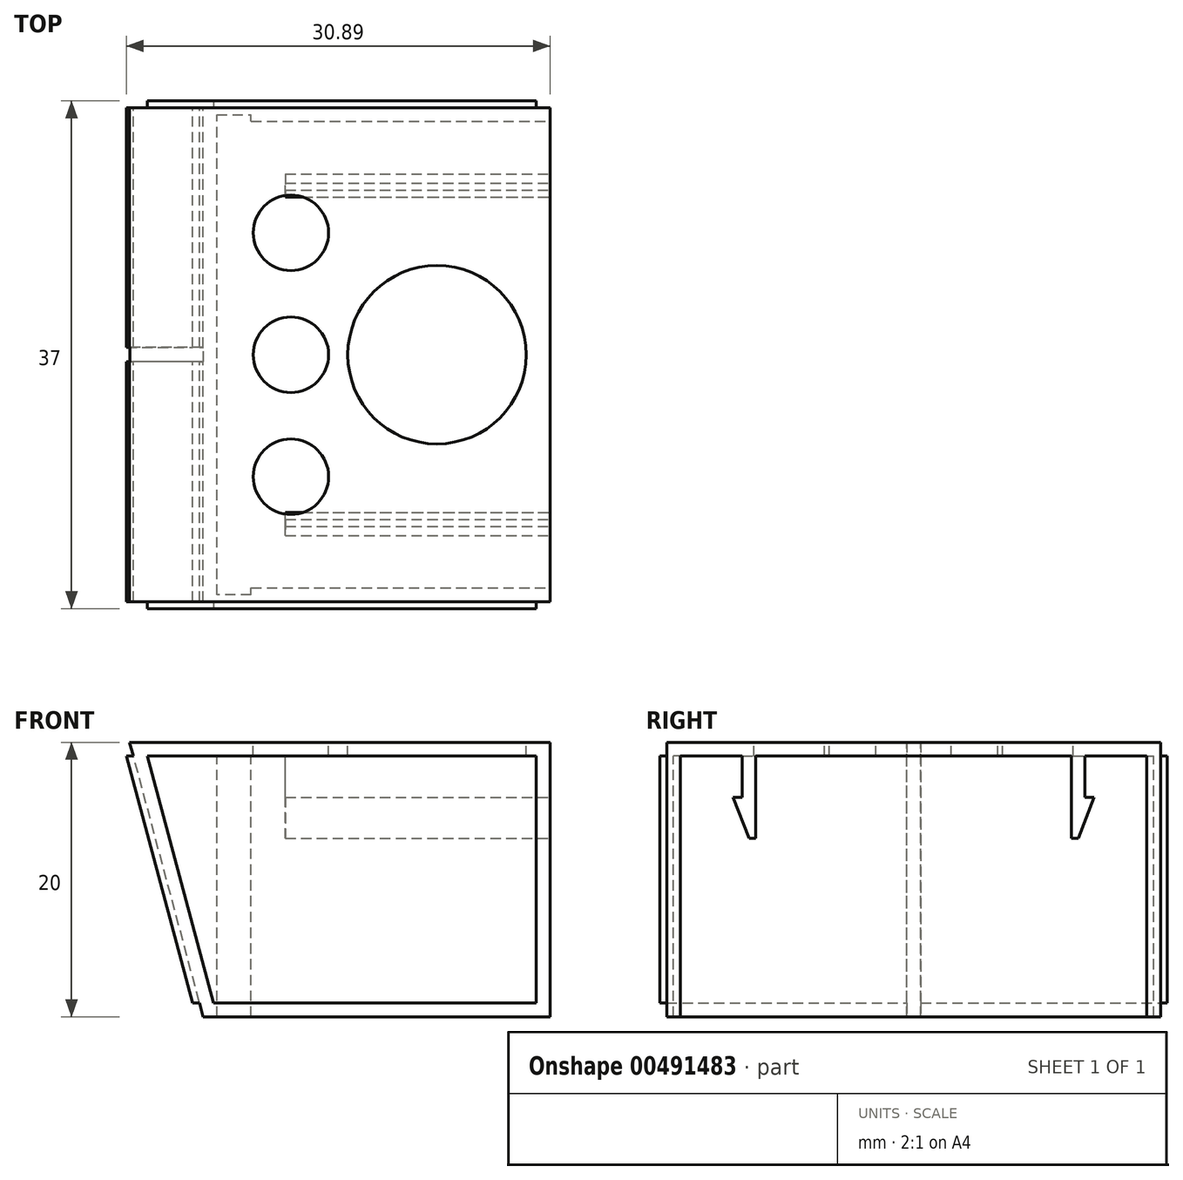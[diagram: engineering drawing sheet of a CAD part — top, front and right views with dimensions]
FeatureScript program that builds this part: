
annotation { "Feature Type Name" : "Feature", "Feature Type Description" : "" }
export const myFeature = defineFeature(function(context is Context, id is Id, definition is map)
    precondition{}
    {
        {
            var Q0;
            Q0=qCreatedBy(makeId("Right.planeOp"),FACE);
            var sketch = newSketch(context, id + "F0", { "sketchPlane" : qUnion([Q0])});
            skLineSegment(sketch, "E0.0", {"start": v(-0.5, 0) * mm, "end": v(-0.5, 19) * mm});
            skLineSegment(sketch, "E1.0", {"start": v(-34.5, 0) * mm, "end": v(-34.5, 19) * mm});
            skLineSegment(sketch, "E2", {"start": v(-34.5, 19) * mm, "end": v(-0.5, 19) * mm});
            skLineSegment(sketch, "E3", {"start": v(-34.5, 0) * mm, "end": v(-0.5, 0) * mm});
            skLineSegment(sketch, "E4.MirrorCS", {"start": v(-30, 16) * mm, "end": v(-30, 19) * mm});
            skLineSegment(sketch, "E5.MirrorCS", {"start": v(-30.67, 16) * mm, "end": v(-30, 16) * mm});
            skLineSegment(sketch, "E6.MirrorCS", {"start": v(-29.5, 13) * mm, "end": v(-30.67, 16) * mm});
            skLineSegment(sketch, "E7.MirrorCS", {"start": v(-29.5, 13) * mm, "end": v(-29, 13) * mm});
            skLineSegment(sketch, "E8.MirrorCS", {"start": v(-29, 13) * mm, "end": v(-29, 19) * mm});
            skLineSegment(sketch, "E9.MirrorCS", {"start": v(-4.33, 16) * mm, "end": v(-5.5, 13) * mm});
            skLineSegment(sketch, "E10.MirrorCS", {"start": v(-4.33, 16) * mm, "end": v(-5, 16) * mm});
            skLineSegment(sketch, "E11.MirrorCS", {"start": v(-5, 16) * mm, "end": v(-5, 19) * mm});
            skLineSegment(sketch, "E12.MirrorCS", {"start": v(-5.5, 13) * mm, "end": v(-6, 13) * mm});
            skLineSegment(sketch, "E13.MirrorCS", {"start": v(-6, 13) * mm, "end": v(-6, 19) * mm});
            skSolve(sketch);
        }
        {
            var Q0;
            Q0=qCreatedBy(makeId("Front.planeOp"),FACE);
            var sketch = newSketch(context, id + "F1", { "sketchPlane" : qUnion([Q0])});
            skLineSegment(sketch, "E14", {"start": v(0, 0) * mm, "end": v(-25.3, 0) * mm});
            skLineSegment(sketch, "E15", {"start": v(-25.3, 0) * mm, "end": v(-30.66, 20) * mm});
            skLineSegment(sketch, "E16", {"start": v(-30.66, 20) * mm, "end": v(0, 20) * mm});
            skLineSegment(sketch, "E17", {"start": v(0, 20) * mm, "end": v(0, 0) * mm});
            skLineSegment(sketch, "E18", {"start": v(-25.3, 0) * mm, "end": v(-38.12, 0) * mm});
            skLineSegment(sketch, "E19", {"start": v(-30.9, 19) * mm, "end": v(-26.07, 1) * mm});
            skPoint(sketch, "E20.orphan", {"position": v(-25.3, -1.87) * mm});
            skLineSegment(sketch, "E21", {"start": v(0, 19) * mm, "end": v(0, 19) * mm});
            skLineSegment(sketch, "E22", {"start": v(-26.07, 1) * mm, "end": v(-25.57, 1) * mm});
            skPoint(sketch, "E23.0.start.orphan", {"position": v(0, 1) * mm});
            skPoint(sketch, "E24.orphan", {"position": v(-29.4, 1) * mm});
            skLineSegment(sketch, "E25", {"start": v(-30.9, 19) * mm, "end": v(-30.4, 19) * mm});
            skLineSegment(sketch, "E26.0", {"start": v(-30.66, 19) * mm, "end": v(-30.4, 19) * mm});
            skLineSegment(sketch, "E27.0", {"start": v(-24.53, 1) * mm, "end": v(-29.36, 19) * mm});
            skLineSegment(sketch, "E28.0", {"start": v(-1, 1) * mm, "end": v(-24.53, 1) * mm});
            skLineSegment(sketch, "E29.0", {"start": v(-1, 19) * mm, "end": v(-1, 1) * mm});
            skLineSegment(sketch, "E30.trimOffspring", {"start": v(-29.36, 19) * mm, "end": v(-1, 19) * mm});
            skLineSegment(sketch, "E31", {"start": v(-30.66, 20) * mm, "end": v(-37.02, 18.3) * mm});
            skSolve(sketch);
        }
        {
            var Q0;
            Q0=makeQuery(id+"F1.imprint","IMPRINT",FACE,{"disambiguationData":[TD([[makeQuery(id+"F1.imprint","IMPRINT",EDGE,{"derivedFrom":sQuery(id+"F1.wireOp",EDGE,"E14")}),-1.0]])]});
            var Q1;
            Q1=makeQuery(id+"F1.imprint","IMPRINT",FACE,{"disambiguationData":[TD([[makeQuery(id+"F1.imprint","IMPRINT",EDGE,{"derivedFrom":sQuery(id+"F1.wireOp",EDGE,"E27.0")}),-1.0]])]});
            var Q2;
            Q2=makeQuery(id+"F1.imprint","IMPRINT",FACE,{"disambiguationData":[TD([[makeQuery(id+"F1.imprint","IMPRINT",EDGE,{"derivedFrom":sQuery(id+"F1.wireOp",EDGE,"E19")}),1.0]])]});
            extrude(context, id + "F2", {"entities" : qUnion([Q0, Q1, Q2]), "depth" : 35.5 * mm, "hasSecondDirection" : true, "secondDirectionOppositeDirection" : true, "secondDirectionDepth" : 0.5 * mm});
        }
        {
            var Q0;
            Q0=makeQuery(id+"F1.imprint","IMPRINT",FACE,{"disambiguationData":[TD([[makeQuery(id+"F1.imprint","IMPRINT",EDGE,{"derivedFrom":sQuery(id+"F1.wireOp",EDGE,"E27.0")}),-1.0]])]});
            extrude(context, id + "F3", {"entities" : qUnion([Q0]), "operationType" : NewBodyOperationType.ADD, "oppositeDirection" : true, "depth" : 1 * mm, "hasSecondDirection" : true, "secondDirectionOppositeDirection" : false, "secondDirectionDepth" : 36 * mm});
        }
        {
            var Q0;
            Q0=makeQuery(id+"F0.imprint","IMPRINT",FACE,{"disambiguationData":[TD([[makeQuery(id+"F0.imprint","IMPRINT",EDGE,{"derivedFrom":sQuery(id+"F0.wireOp",EDGE,"32d8cbf2-fb97-4c8f-9446-bffa937a5d3c.0")}),1.0]])]});
            var Q1;
            {var subQ3=sQuery(id+"F0.wireOp",EDGE,"E0.0");Q1=makeQuery(id+"F0.imprint","IMPRINT",FACE,{"disambiguationData":[TD([[makeQuery(id+"F0.imprint","IMPRINT",EDGE,{"derivedFrom":subQ3}),1.0]])]});}
            extrude(context, id + "F4", {"entities" : qUnion([Q0, Q1]), "operationType" : NewBodyOperationType.REMOVE, "oppositeDirection" : true, "depth" : 24.3 * mm});
        }
        {
            var Q0;
            Q0=sQuery(id+"F1.wireOp",VERTEX,"E31.end");
            var Q1;
            Q1=sQuery(id+"F1.wireOp",VERTEX,"E16.start");
            var Q2;
            Q2=makeQuery(id+"F2.opExtrude","CAP_VERTEX",VERTEX,{"disambiguationData":[OSD([sQuery(id+"F1.wireOp",EDGE,"E15"),sQuery(id+"F1.wireOp",EDGE,"E16")])],"isStart":false});
            cPlane(context, id + "F5", {"entities" : qUnion([Q0, Q1, Q2]), "cplaneType" : CPlaneType.THREE_POINT, "offset" : 25 * mm, "width" : 150 * mm, "height" : 150 * mm});
        }
        {
            var Q0;
            Q0=qCreatedBy(id+"F5.planeOp",FACE);
            var sketch = newSketch(context, id + "F6", { "sketchPlane" : qUnion([Q0])});
            skLineSegment(sketch, "E32.0", {"start": v(-24.43, -1) * mm, "end": v(-24.93, -1) * mm});
            skLineSegment(sketch, "E33.0", {"start": v(-24.43, -34) * mm, "end": v(-24.93, -34) * mm});
            skLineSegment(sketch, "E34.0", {"start": v(-24.43, -16.97) * mm, "end": v(-24.93, -16.97) * mm});
            skLineSegment(sketch, "E35.0", {"start": v(-24.43, -18) * mm, "end": v(-24.93, -18) * mm});
            skLineSegment(sketch, "E36.trimOffspring", {"start": v(-24.93, -16.97) * mm, "end": v(-24.93, -18) * mm});
            skLineSegment(sketch, "E37.trimOffspring", {"start": v(-24.43, -16.97) * mm, "end": v(-24.43, -18) * mm});
            skLineSegment(sketch, "E38.0", {"start": v(-24.43, 0.5) * mm, "end": v(-24.93, 0.5) * mm});
            skLineSegment(sketch, "E39", {"start": v(-24.93, 0.5) * mm, "end": v(-24.93, -1) * mm});
            skLineSegment(sketch, "E40", {"start": v(-24.43, -1) * mm, "end": v(-24.43, 0.5) * mm});
            skLineSegment(sketch, "E41.0", {"start": v(-24.43, -35.5) * mm, "end": v(-24.93, -35.5) * mm});
            skLineSegment(sketch, "E42", {"start": v(-24.93, -34) * mm, "end": v(-24.93, -35.5) * mm});
            skLineSegment(sketch, "E43", {"start": v(-24.43, -35.5) * mm, "end": v(-24.43, -34) * mm});
            skSolve(sketch);
        }
        {
            var Q0;
            Q0=makeQuery(id+"F6.imprint","IMPRINT",FACE,{"disambiguationData":[TD([[makeQuery(id+"F6.imprint","IMPRINT",EDGE,{"derivedFrom":sQuery(id+"F6.wireOp",EDGE,"9PfR2qlM-xlqo-y65q-UvL4-z1dMFV8YH0sN")}),-1.0]])]});
            var Q1;
            Q1=makeQuery(id+"F6.imprint","IMPRINT",FACE,{"disambiguationData":[TD([[makeQuery(id+"F6.imprint","IMPRINT",EDGE,{"derivedFrom":sQuery(id+"F6.wireOp",EDGE,"E34.0")}),1.0]])]});
            var Q2;
            Q2=makeQuery(id+"F6.imprint","IMPRINT",FACE,{"disambiguationData":[TD([[makeQuery(id+"F6.imprint","IMPRINT",EDGE,{"derivedFrom":sQuery(id+"F6.wireOp",EDGE,"ddf47fad-d214-44eb-bef5-dcffc066888e.0")}),-1.0]])]});
            extrude(context, id + "F7", {"entities" : qUnion([Q0, Q1, Q2]), "operationType" : NewBodyOperationType.REMOVE, "oppositeDirection" : true, "depth" : 25 * mm});
        }
        {
            var Q0;
            Q0=makeQuery(id+"F2.opExtrude","SWEPT_FACE",FACE,{"disambiguationData":[OSD([sQuery(id+"F1.wireOp",EDGE,"E16")])]});
            var sketch = newSketch(context, id + "F8", { "sketchPlane" : qUnion([Q0])});
            skLineSegment(sketch, "E44", {"start": v(0, 0.5) * mm, "end": v(0, -35.5) * mm});
            skLineSegment(sketch, "E45.0", {"start": v(-24.3, 0) * mm, "end": v(-24.3, -35) * mm});
            skLineSegment(sketch, "E46.0", {"start": v(-20.3, -7.34) * mm, "end": v(-20.3, -9.88) * mm});
            skLineSegment(sketch, "E47.0", {"start": v(-18.9, -7.34) * mm, "end": v(-18.9, -9.88) * mm});
            skLineSegment(sketch, "E48", {"start": v(-20.3, -17.5) * mm, "end": v(-18.9, -17.5) * mm});
            skLineSegment(sketch, "E49.0", {"start": v(-20.3, -9.88) * mm, "end": v(-18.9, -9.88) * mm});
            skLineSegment(sketch, "E50.0", {"start": v(-20.3, -25.12) * mm, "end": v(-18.9, -25.12) * mm});
            skLineSegment(sketch, "E51.0", {"start": v(-20.3, -7.34) * mm, "end": v(-18.9, -7.34) * mm});
            skLineSegment(sketch, "E52.0", {"start": v(-20.3, -27.66) * mm, "end": v(-18.9, -27.66) * mm});
            skPoint(sketch, "E53.orphan", {"position": v(-18.9, 0) * mm});
            skPoint(sketch, "E54.orphan", {"position": v(-20.3, 0) * mm});
            skLineSegment(sketch, "E55.trimOffspring", {"start": v(-20.3, -25.12) * mm, "end": v(-20.3, -27.66) * mm});
            skLineSegment(sketch, "E56.trimOffspring", {"start": v(-18.9, -25.12) * mm, "end": v(-18.9, -27.66) * mm});
            skPoint(sketch, "E57.orphan", {"position": v(-20.3, -35) * mm});
            skPoint(sketch, "E58.orphan", {"position": v(-18.9, -35) * mm});
            skCircle(sketch, "E59", {"center": v(-18.9, -26.39) * mm, "radius": 2.75 * mm});
            skCircle(sketch, "E60", {"center": v(-18.9, -8.61) * mm, "radius": 2.75 * mm});
            skCircle(sketch, "E61", {"center": v(-18.9, -17.5) * mm, "radius": 2.75 * mm});
            skLineSegment(sketch, "E62", {"start": v(-18.9, -17.5) * mm, "end": v(-8.25, -17.5) * mm});
            skCircle(sketch, "E63", {"center": v(-8.25, -17.5) * mm, "radius": 6.5 * mm});
            skLineSegment(sketch, "E64.0", {"start": v(-21.8, 0) * mm, "end": v(-21.8, -35) * mm});
            skLineSegment(sketch, "E65", {"start": v(-24.3, -35) * mm, "end": v(-21.8, -35) * mm});
            skLineSegment(sketch, "E66", {"start": v(-21.8, 0) * mm, "end": v(-24.3, 0) * mm});
            skLineSegment(sketch, "E67.0", {"start": v(-24.3, -34.5) * mm, "end": v(-21.8, -34.5) * mm});
            skLineSegment(sketch, "E68.0", {"start": v(-21.8, -0.5) * mm, "end": v(-24.3, -0.5) * mm});
            skSolve(sketch);
        }
        {
            var Q0;
            Q0=makeQuery(id+"F8.imprint","IMPRINT",FACE,{"disambiguationData":[TD([[makeQuery(id+"F8.imprint","IMPRINT",EDGE,{"derivedFrom":sQuery(id+"F8.wireOp",EDGE,"E46.0")}),-1.0]])]});
            var Q1;
            Q1=makeQuery(id+"F8.imprint","IMPRINT",FACE,{"disambiguationData":[TD([[makeQuery(id+"F8.imprint","IMPRINT",EDGE,{"derivedFrom":sQuery(id+"F8.wireOp",EDGE,"E46.0")}),1.0]])]});
            var Q2;
            Q2=makeQuery(id+"F8.imprint","IMPRINT",FACE,{"disambiguationData":[TD([[makeQuery(id+"F8.imprint","IMPRINT",EDGE,{"derivedFrom":sQuery(id+"F8.wireOp",EDGE,"E61")}),1.0]])]});
            var Q3;
            Q3=makeQuery(id+"F8.imprint","IMPRINT",FACE,{"disambiguationData":[TD([[makeQuery(id+"F8.imprint","IMPRINT",EDGE,{"derivedFrom":sQuery(id+"F8.wireOp",EDGE,"E50.0")}),1.0]])]});
            var Q4;
            Q4=makeQuery(id+"F8.imprint","IMPRINT",FACE,{"disambiguationData":[TD([[makeQuery(id+"F8.imprint","IMPRINT",EDGE,{"derivedFrom":sQuery(id+"F8.wireOp",EDGE,"E63")}),1.0]])]});
            var Q5;
            Q5=makeQuery(id+"F8.imprint","IMPRINT",FACE,{"disambiguationData":[TD([[makeQuery(id+"F8.imprint","IMPRINT",EDGE,{"derivedFrom":sQuery(id+"F8.wireOp",EDGE,"E50.0")}),-1.0]])]});
            var Q6;
            {var subQ0=sQuery(id+"F0.wireOp",EDGE,"E2");Q6=makeQuery(id+"F4.boolean.opBoolean","COPY",FACE,{"derivedFrom":makeQuery(id+"F4.opExtrude","SWEPT_FACE",FACE,{"disambiguationData":[OSD([subQ0]),TDD([makeQuery(id+"F0.imprint","IMPRINT",EDGE,{"disambiguationData":[TD([[makeQuery(id+"F0.imprint","INTERSECT",VERTEX,{"derivedFrom":[sQuery(id+"F0.wireOp",EDGE,"029f2400-b672-4e93-a4e7-b8ca7ef6a9fd.0"),subQ0]}),1.0]])],"derivedFrom":subQ0})])]})});}
            extrude(context, id + "F9", {"entities" : qUnion([Q0, Q1, Q2, Q3, Q4, Q5]), "operationType" : NewBodyOperationType.REMOVE, "endBound" : BoundingType.UP_TO_SURFACE, "oppositeDirection" : true, "endBoundEntityFace" : qUnion([Q6]), "depth" : 25 * mm});
        }
        {
            var Q0;
            {var subQ1=sQuery(id+"F0.wireOp",EDGE,"e70d791c-1034-4ed7-ba50-f73bdf0bc0440.MirrorCS");Q0=makeQuery(id+"F0.imprint","IMPRINT",FACE,{"disambiguationData":[TD([[makeQuery(id+"F0.imprint","IMPRINT",EDGE,{"derivedFrom":subQ1}),1.0]])]});}
            var Q1;
            {var subQ1=sQuery(id+"F0.wireOp",EDGE,"5876fb81-047d-4f3c-aed5-0b9b1cf505e90.MirrorCS");Q1=makeQuery(id+"F0.imprint","IMPRINT",FACE,{"disambiguationData":[TD([[makeQuery(id+"F0.imprint","IMPRINT",EDGE,{"derivedFrom":subQ1}),-1.0]])]});}
            var Q2;
            {var subQ0=sQuery(id+"F0.wireOp",EDGE,"E4.MirrorCS");Q2=makeQuery(id+"F0.imprint","IMPRINT",FACE,{"disambiguationData":[TD([[makeQuery(id+"F0.imprint","IMPRINT",EDGE,{"derivedFrom":subQ0}),-1.0]])]});}
            var Q3;
            Q3=makeQuery(id+"F0.imprint","IMPRINT",FACE,{"disambiguationData":[TD([[makeQuery(id+"F0.imprint","IMPRINT",EDGE,{"derivedFrom":sQuery(id+"F0.wireOp",EDGE,"E9.MirrorCS")}),-1.0]])]});
            var Q4;
            Q4=makeQuery(id+"F4.boolean.opBoolean","COPY",FACE,{"derivedFrom":makeQuery(id+"F4.opExtrude","CAP_FACE",FACE,{"disambiguationData":[OSD([sQuery(id+"F0.wireOp",EDGE,"E0.0"),sQuery(id+"F0.wireOp",EDGE,"E1.0"),sQuery(id+"F0.wireOp",EDGE,"E2"),sQuery(id+"F0.wireOp",EDGE,"E3"),sQuery(id+"F0.wireOp",EDGE,"5876fb81-047d-4f3c-aed5-0b9b1cf505e90.MirrorCS"),sQuery(id+"F0.wireOp",EDGE,"a7f62685-10dd-4fd1-b528-79ccf468192d0.MirrorCS"),sQuery(id+"F0.wireOp",EDGE,"7f09e340-4616-42ec-a4bb-6f3a67d284dc0.MirrorCS"),sQuery(id+"F0.wireOp",EDGE,"40ba5f29-6dcd-4d71-a628-9ff452c9a6c70.MirrorCS"),sQuery(id+"F0.wireOp",EDGE,"2152234d-400f-4cc2-8a55-b5b9fa8d43900.MirrorCS"),sQuery(id+"F0.wireOp",EDGE,"e70d791c-1034-4ed7-ba50-f73bdf0bc0440.MirrorCS"),sQuery(id+"F0.wireOp",EDGE,"6097c497-a0a3-485f-ac21-d0f877e35bc30.MirrorCS"),sQuery(id+"F0.wireOp",EDGE,"ee57d7c9-d907-4d31-ba06-7bcf47c301ab0.MirrorCS"),sQuery(id+"F0.wireOp",EDGE,"b0bb755d-e530-45c8-a6da-76c959a20c690.MirrorCS"),sQuery(id+"F0.wireOp",EDGE,"6a8256c7-6e58-46d3-948a-d5775b9872240.MirrorCS")])],"isStart":false})});
            extrude(context, id + "F10", {"entities" : qUnion([Q0, Q1, Q2, Q3]), "operationType" : NewBodyOperationType.REMOVE, "endBound" : BoundingType.UP_TO_SURFACE, "oppositeDirection" : true, "endBoundEntityFace" : qUnion([Q4]), "depth" : 20 * mm, "hasSecondDirection" : true, "secondDirectionOppositeDirection" : true, "secondDirectionDepth" : 19.3 * mm});
        }
        {
            var Q0;
            {var subQ0=sQuery(id+"F8.wireOp",EDGE,"E65");Q0=makeQuery(id+"F8.imprint","IMPRINT",FACE,{"disambiguationData":[TD([[makeQuery(id+"F8.imprint","IMPRINT",EDGE,{"derivedFrom":subQ0}),1.0]])]});}
            var Q1;
            {var subQ0=sQuery(id+"F8.wireOp",EDGE,"E66");Q1=makeQuery(id+"F8.imprint","IMPRINT",FACE,{"disambiguationData":[TD([[makeQuery(id+"F8.imprint","IMPRINT",EDGE,{"derivedFrom":subQ0}),1.0]])]});}
            extrude(context, id + "F11", {"entities" : qUnion([Q0, Q1]), "operationType" : NewBodyOperationType.REMOVE, "oppositeDirection" : true, "depth" : 25 * mm, "hasSecondDirection" : true, "secondDirectionOppositeDirection" : true, "secondDirectionDepth" : 1 * mm});
        }
    });
